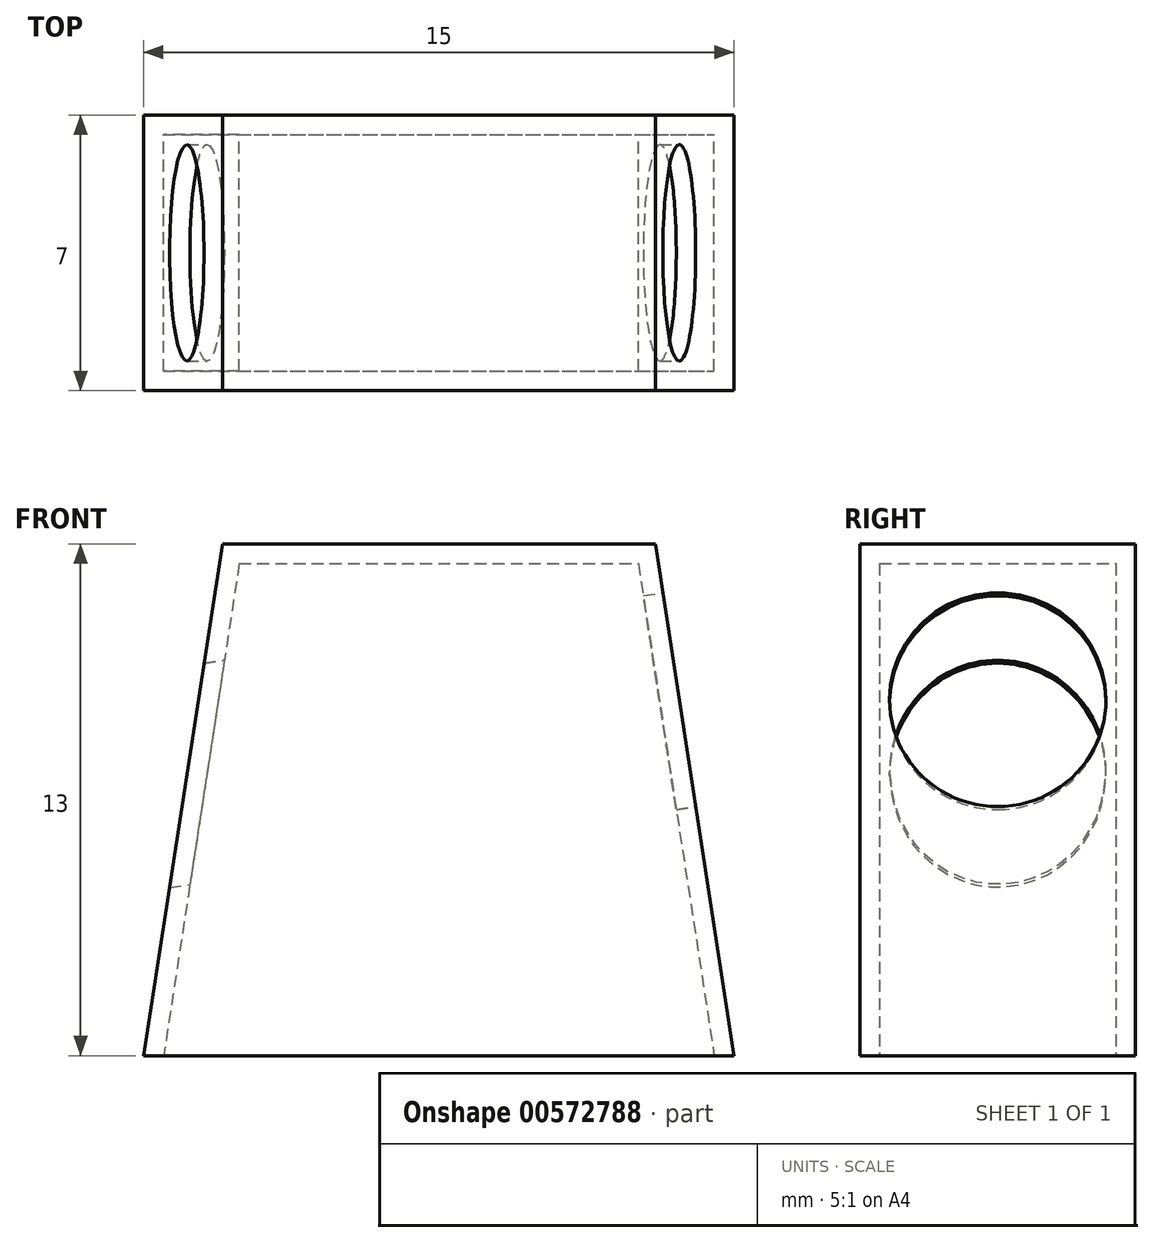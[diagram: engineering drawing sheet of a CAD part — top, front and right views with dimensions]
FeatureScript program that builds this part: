
annotation { "Feature Type Name" : "Feature", "Feature Type Description" : "" }
export const myFeature = defineFeature(function(context is Context, id is Id, definition is map)
    precondition{}
    {
        {
            var Q0;
            Q0=qCreatedBy(makeId("Front.planeOp"),FACE);
            var sketch = newSketch(context, id + "F0", { "sketchPlane" : qUnion([Q0])});
            skLineSegment(sketch, "E0", {"start": v(-7.5, 0) * mm, "end": v(7.5, 0) * mm});
            skLineSegment(sketch, "E1", {"start": v(-5.5, 13) * mm, "end": v(5.5, 13) * mm});
            skLineSegment(sketch, "E2", {"start": v(5.5, 13) * mm, "end": v(7.5, 0) * mm});
            skLineSegment(sketch, "E3", {"start": v(-5.5, 13) * mm, "end": v(-7.5, 0) * mm});
            skSolve(sketch);
        }
        {
            var Q0;
            Q0 = qSketchRegion(id + "F0", true);
            extrude(context, id + "F1", {"entities" : qUnion([Q0]), "endBound" : BoundingType.SYMMETRIC, "depth" : 7 * mm, "offsetDistance" : 25.4 * mm});
        }
        {
            var Q0;
            Q0=makeQuery(id+"F1.opExtrude","SWEPT_FACE",FACE,{"disambiguationData":[OSD([sQuery(id+"F0.wireOp",EDGE,"E0")])]});
            shell(context, id + "F2", {"entities" : qUnion([Q0]), "thickness" : .5 * mm});
        }
        {
            var Q0;
            Q0=makeQuery(id+"F1.opExtrude","SWEPT_FACE",FACE,{"disambiguationData":[OSD([sQuery(id+"F0.wireOp",EDGE,"E2")])]});
            var sketch = newSketch(context, id + "F3", { "sketchPlane" : qUnion([Q0])});
            skCircle(sketch, "E4", {"center": v(0, 8.01) * mm, "radius": 2 * mm});
            skSolve(sketch);
        }
        {
            var Q0;
            Q0=sQuery(id+"F3.wireOp",VERTEX,"E4.center");
            var Q1;
            Q1=makeQuery(id+"F1.opExtrude","SWEPT_BODY",BODY,{"disambiguationData":[OSD([sQuery(id+"F0.wireOp",EDGE,"E0"),sQuery(id+"F0.wireOp",EDGE,"E1"),sQuery(id+"F0.wireOp",EDGE,"E2"),sQuery(id+"F0.wireOp",EDGE,"E3")])]});
            hole(context, id + "F4", {"style" : HoleStyle.SIMPLE, "endStyle" : HoleEndStyle.THROUGH, "standardTappedOrClearance" : lookupTablePath({ "standard" : "ISO", "fit" : "Normal", "size" : "M5", "type" : "Clearance" }), "standardBlindInLast" : lookupTablePath({ "fit" : "Standard", "standard" : "ISO", "size" : "M5", "type" : "Clearance" }), "holeDiameter" : 5.5 * mm, "isTappedThrough" : true, "tappedDepth" : 12.7 * mm, "tapClearance" : 3, "locations" : qUnion([Q0]), "scope" : qUnion([Q1])});
        }
    });
